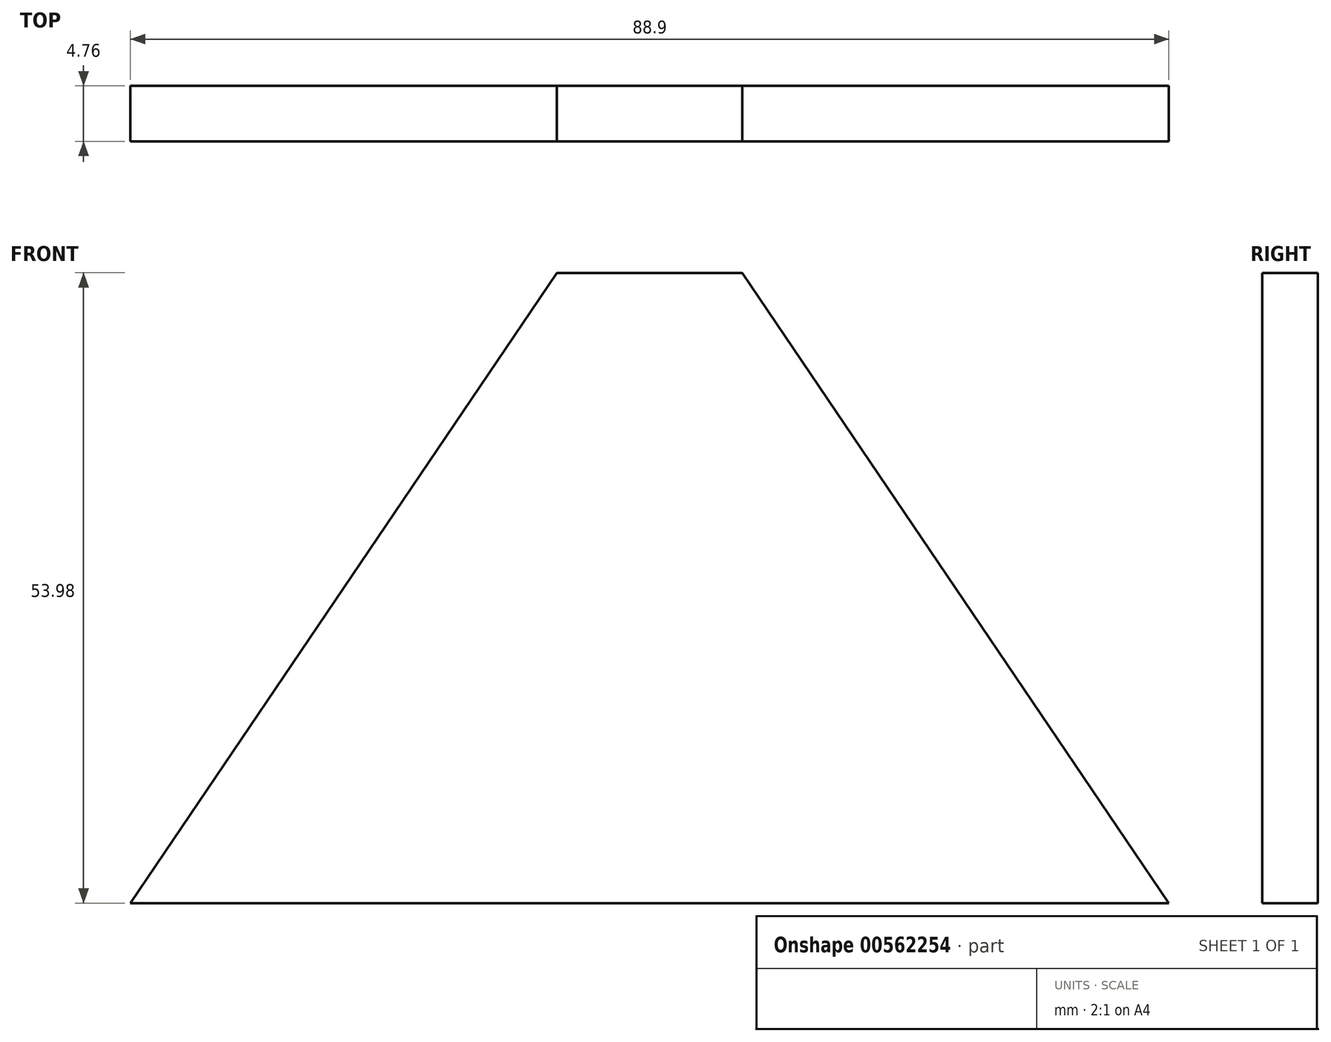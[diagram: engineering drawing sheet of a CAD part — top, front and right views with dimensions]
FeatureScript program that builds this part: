
annotation { "Feature Type Name" : "Feature", "Feature Type Description" : "" }
export const myFeature = defineFeature(function(context is Context, id is Id, definition is map)
    precondition{}
    {
        {
            var Q0;
            Q0=qCreatedBy(makeId("Front.planeOp"),FACE);
            var sketch = newSketch(context, id + "F0", { "sketchPlane" : qUnion([Q0])});
            skLineSegment(sketch, "E0", {"start": v(44.45, 0) * mm, "end": v(-44.45, 0) * mm});
            skLineSegment(sketch, "E1", {"start": v(-44.45, 0) * mm, "end": v(-7.94, 53.97) * mm});
            skLineSegment(sketch, "E2.MirrorCS", {"start": v(44.45, 0) * mm, "end": v(7.94, 53.98) * mm});
            skLineSegment(sketch, "E3", {"start": v(-7.94, 53.97) * mm, "end": v(7.94, 53.97) * mm});
            skSolve(sketch);
        }
        {
            var Q0;
            Q0 = qSketchRegion(id + "F0", true);
            extrude(context, id + "F1", {"entities" : qUnion([Q0]), "depth" : 4.76 * mm, "offsetDistance" : 25.4 * mm});
        }
    });
